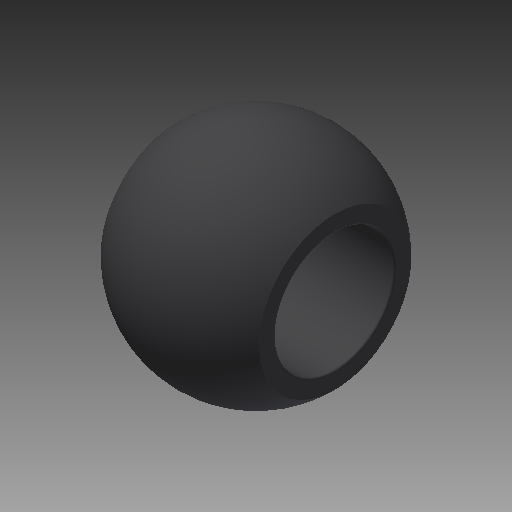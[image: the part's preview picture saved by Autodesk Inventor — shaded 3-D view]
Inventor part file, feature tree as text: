
AUTODESK INVENTOR PART (.ipt)
format: ipt  version: 2018 (Build 220112000, 112)  size: 152,576 bytes
history: native  units: mm
features: other x7, revolve x1, sketch x1
ambient origin geometry x8: Origin, YZ Plane, XZ Plane, XY Plane, X Axis, Y Axis, Z Axis, Center Point
bodies: Solid1 (feature_tree)
feature tree (9):
  revolve  "Revolution1"  [1 undecoded]
  other  "IP1_XY"
  other  "IP1_YZ"
  other  "IP1_ZX"
  other  "IP1_X"
  other  "IP1_Y"
  other  "IP1_Z"
  other  "IP1_Center"
  sketch  "Sketch_1"  dims[d0=360.0deg]
note: 1 required parameter value undecoded (feature->parameter linkage not recoverable at this tier; creation-order binding heuristic only, values carry confidence <= 0.55)
